# Revit family: Filter-Navien-NaviClean-GXXX001727
name_source: partatom
category: Mechanical Equipment
revit_build: Autodesk Revit 2017 (Build: 20160225_1515(x64)
units: mm (PartAtom-declared; Revit-internal decimal feet)

## family parameters
Cut with Voids When Loaded = No
Host = Face
OmniClass Number = 23.45.55.21
OmniClass Title = Drains (Wastes)
Part Type = Normal
Room Calculation Point = No
Round Connector Dimension = Use Diameter
Shared = No

## types (1)
- NaviClean - GXXX001727
    Default Elevation = 48 "
    Depth = 4.21 "
    Description = Magnetic Boiler Filter
    Finish = Plastic - Navien - Black
    Height = 10.28 "
    Installation Type = The NaviClean Magnetic Boiler Filter can be installed anywhere on the main system piping. To achieve best performance, it is recommended that the NaviClean be installed after the last heating zone and before the boiler. NaviClean is also fully compatible with Adey chemicals.
    Manufacturer = Navien, Inc.
    Manufacturer Fax Number = (949) 420-0430
    Model = GXXX001727
    Product Documentation Link = https://www.navieninc.com
    Product Name = NaviClean
    Product Page URL = https://www.navieninc.com
    URL = https://www.navieninc.com
    Version = 2017 - v1.0.a
    Weight = 7.50 lbf
    Width = 3.15 "

## geometry (parser evidence)
native form markers: Sweep x3
no freeform markers — native parametric forms only
